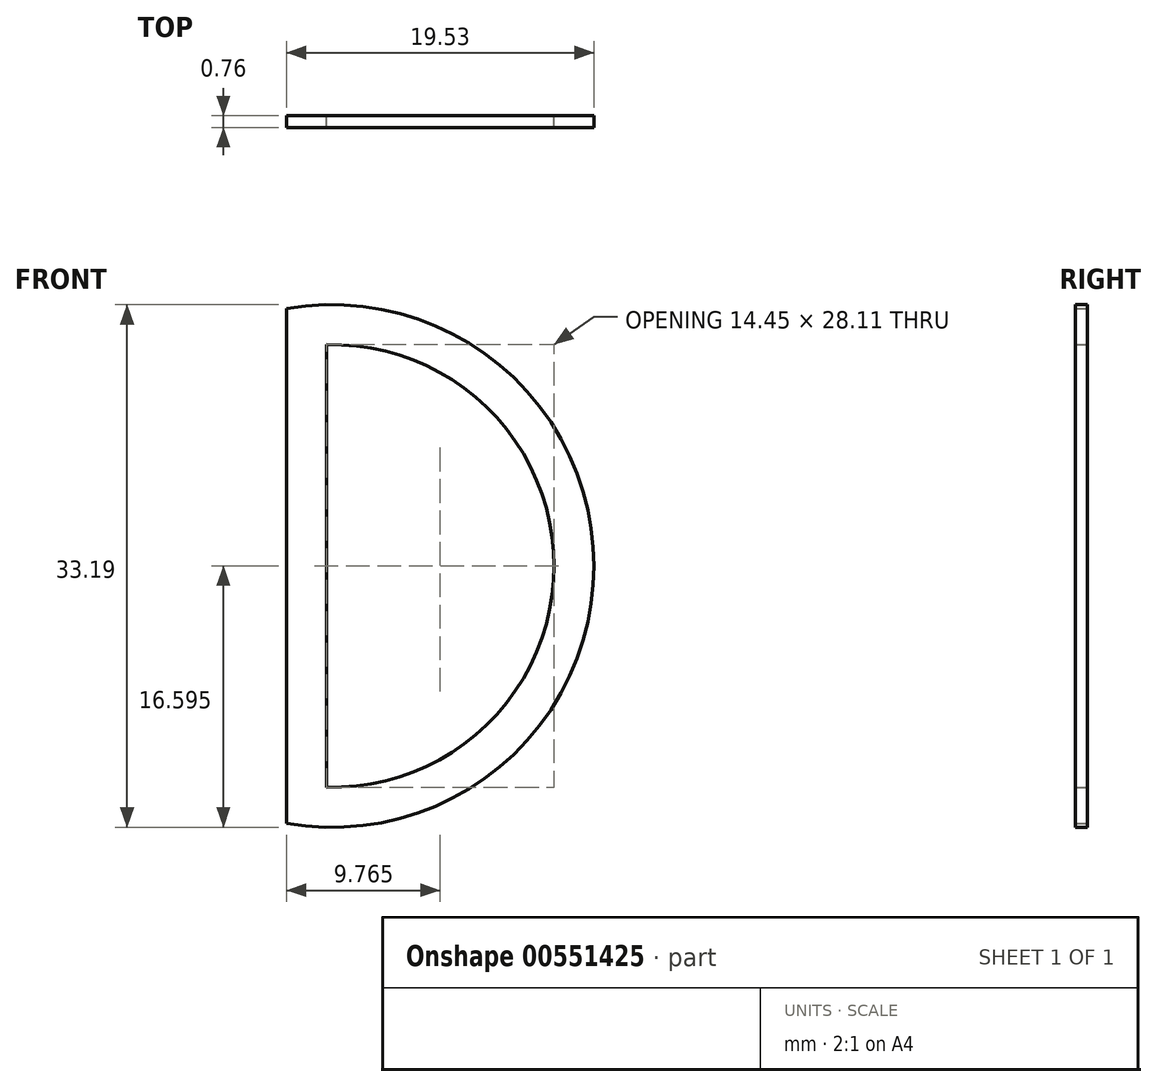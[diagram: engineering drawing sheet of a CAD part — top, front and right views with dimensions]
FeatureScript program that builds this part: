
annotation { "Feature Type Name" : "Feature", "Feature Type Description" : "" }
export const myFeature = defineFeature(function(context is Context, id is Id, definition is map)
    precondition{}
    {
        {
            var Q0;
            Q0=qCreatedBy(makeId("Front.planeOp"),FACE);
            var sketch = newSketch(context, id + "F0", { "sketchPlane" : qUnion([Q0])});
            skLineSegment(sketch, "E0", {"start": v(0, 16.03) * mm, "end": v(0, -16.64) * mm});
            skArc(sketch, "E1", {"start": v(0, -16.64) * mm, "mid": v(19.53, -0.3) * mm, "end": v(0, 16.03) * mm});
            skArc(sketch, "E2", {"start": v(0, -16.64) * mm, "mid": v(14.53, -0.3) * mm, "end": v(0, 16.03) * mm});
            skSolve(sketch);
        }
        {
            var Q0;
            Q0 = qSketchRegion(id + "F0", true);
            extrude(context, id + "F1", {"entities" : qUnion([Q0]), "depth" : 0.76 * mm, "offsetDistance" : 25.4 * mm});
        }
        {
            var Q0;
            Q0=makeQuery(id+"F1.opExtrude","CAP_FACE",FACE,{"disambiguationData":[OSD([sQuery(id+"F0.wireOp",EDGE,"E0"),sQuery(id+"F0.wireOp",EDGE,"E1")])],"isStart":true});
            var Q1;
            Q1=makeQuery(id+"F1.opExtrude","CAP_FACE",FACE,{"disambiguationData":[OSD([sQuery(id+"F0.wireOp",EDGE,"E0"),sQuery(id+"F0.wireOp",EDGE,"E1")])],"isStart":false});
            shell(context, id + "F2", {"entities" : qUnion([Q0, Q1]), "thickness" : 2.54 * mm});
        }
    });
